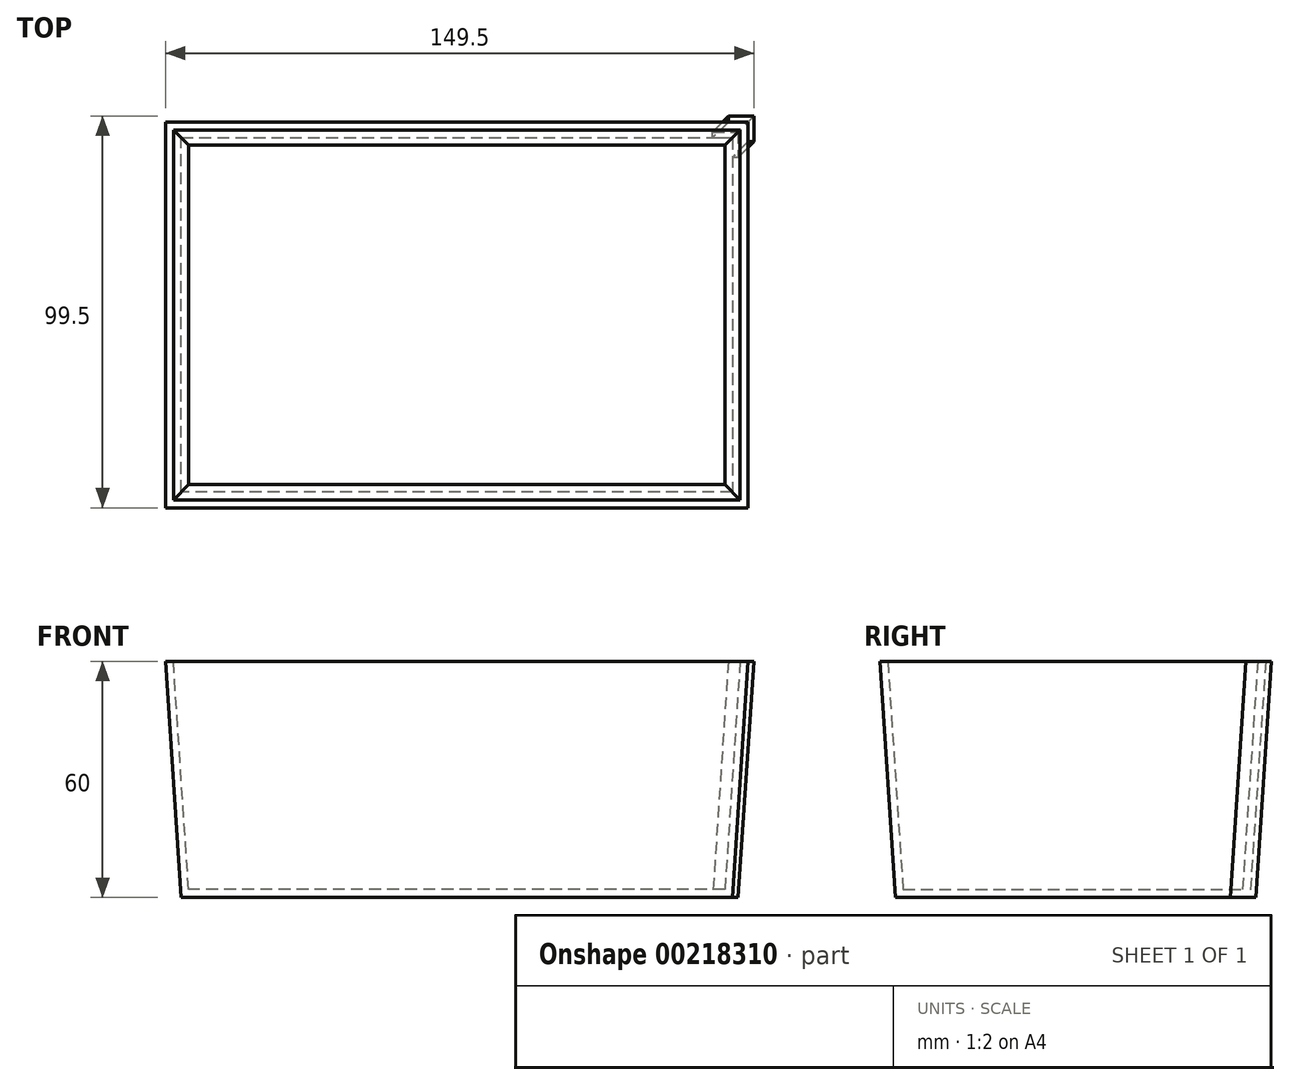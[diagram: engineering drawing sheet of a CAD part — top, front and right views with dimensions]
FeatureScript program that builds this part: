
annotation { "Feature Type Name" : "Feature", "Feature Type Description" : "" }
export const myFeature = defineFeature(function(context is Context, id is Id, definition is map)
    precondition{}
    {
        {
            var Q0;
            Q0=qCreatedBy(makeId("Top.planeOp"),FACE);
            var sketch = newSketch(context, id + "F0", { "sketchPlane" : qUnion([Q0])});
            skLineSegment(sketch, "E0.bottom", {"start": v(75, -50) * mm, "end": v(-75, -50) * mm});
            skLineSegment(sketch, "E0.top", {"start": v(75, 50) * mm, "end": v(-75, 50) * mm});
            skLineSegment(sketch, "E0.left", {"start": v(75, -50) * mm, "end": v(75, 50) * mm});
            skLineSegment(sketch, "E0.right", {"start": v(-75, -50) * mm, "end": v(-75, 50) * mm});
            skPoint(sketch, "E0.middle", {"position": v(0, 0) * mm});
            skSolve(sketch);
        }
        {
            var Q0;
            Q0 = qSketchRegion(id + "F0", true);
            extrude(context, id + "F1", {"entities" : qUnion([Q0]), "depth" : 60 * mm, "offsetDistance" : 25 * mm});
        }
        {
            var Q0;
            Q0=makeQuery(id+"F1.opExtrude","CAP_FACE",FACE,{"disambiguationData":[OSD([sQuery(id+"F0.wireOp",EDGE,"E0.bottom"),sQuery(id+"F0.wireOp",EDGE,"E0.top"),sQuery(id+"F0.wireOp",EDGE,"E0.left"),sQuery(id+"F0.wireOp",EDGE,"E0.right")])],"isStart":true});
            chamfer(context, id + "F2", {"entities" : qUnion([Q0]), "chamferType" : ChamferType.TWO_OFFSETS, "width1" : 5 * mm, "oppositeDirection" : false, "width2" : 75 * mm, "tangentPropagation" : true});
        }
        {
            var Q0;
            Q0=makeQuery(id+"F1.opExtrude","CAP_FACE",FACE,{"disambiguationData":[OSD([sQuery(id+"F0.wireOp",EDGE,"E0.bottom"),sQuery(id+"F0.wireOp",EDGE,"E0.top"),sQuery(id+"F0.wireOp",EDGE,"E0.left"),sQuery(id+"F0.wireOp",EDGE,"E0.right")])],"isStart":false});
            shell(context, id + "F3", {"entities" : qUnion([Q0]), "thickness" : 2 * mm});
        }
        {
            var Q0;
            Q0=makeQuery(id+"F1.opExtrude","CAP_FACE",FACE,{"disambiguationData":[OSD([sQuery(id+"F0.wireOp",EDGE,"E0.bottom"),sQuery(id+"F0.wireOp",EDGE,"E0.top"),sQuery(id+"F0.wireOp",EDGE,"E0.left"),sQuery(id+"F0.wireOp",EDGE,"E0.right")])],"isStart":false});
            var sketch = newSketch(context, id + "F4", { "sketchPlane" : qUnion([Q0])});
            skLineSegment(sketch, "E1", {"start": v(74, 49) * mm, "end": v(69, 49) * mm});
            skLineSegment(sketch, "E2", {"start": v(69, 49) * mm, "end": v(69, 50.5) * mm});
            skLineSegment(sketch, "E3", {"start": v(69, 50.5) * mm, "end": v(75.5, 50.5) * mm});
            skLineSegment(sketch, "E4", {"start": v(75.5, 50.5) * mm, "end": v(75.5, 44) * mm});
            skLineSegment(sketch, "E5", {"start": v(75.5, 44) * mm, "end": v(74, 44) * mm});
            skLineSegment(sketch, "E6", {"start": v(74, 44) * mm, "end": v(74, 49) * mm});
            skSolve(sketch);
        }
        {
            var Q0;
            Q0 = qSketchRegion(id + "F4", true);
            var Q1;
            Q1=makeQuery(id+"F2.opChamfer","BLEND_EDGE",EDGE,{"blendedFrom":[makeQuery(id+"F1.opExtrude","CAP_EDGE",EDGE,{"disambiguationData":[OSD([sQuery(id+"F0.wireOp",EDGE,"E0.top")])],"isStart":true}),makeQuery(id+"F1.opExtrude","CAP_EDGE",EDGE,{"disambiguationData":[OSD([sQuery(id+"F0.wireOp",EDGE,"E0.left")])],"isStart":true})],"blendedInto":[]});
            sweep(context, id + "F5", {"profiles" : qUnion([Q0]), "path" : qUnion([Q1])});
        }
    });
